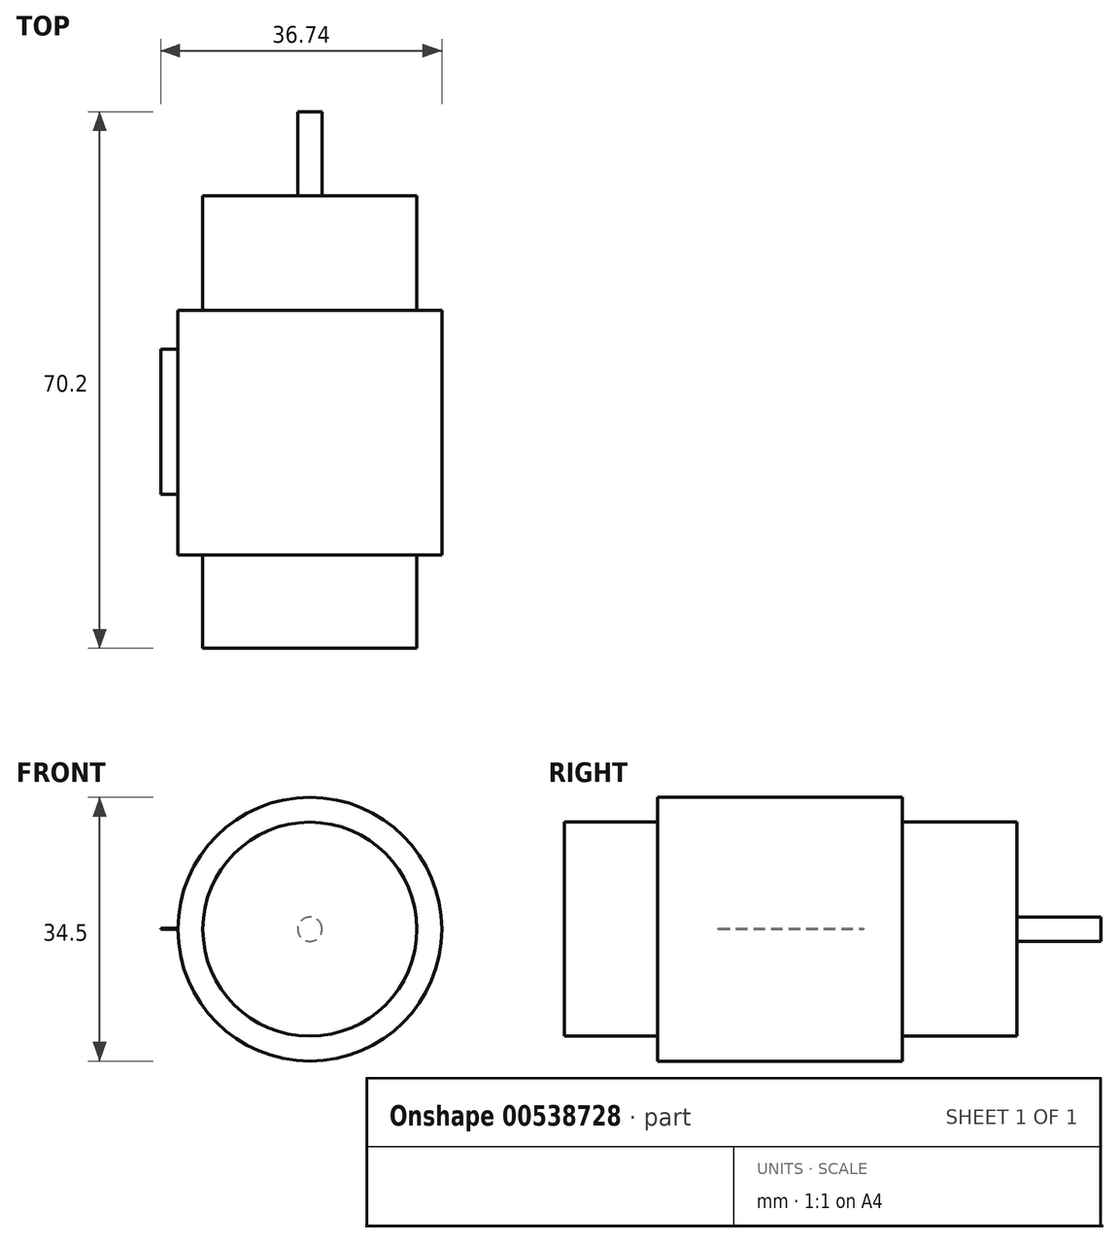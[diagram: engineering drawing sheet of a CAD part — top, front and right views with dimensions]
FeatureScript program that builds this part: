
annotation { "Feature Type Name" : "Feature", "Feature Type Description" : "" }
export const myFeature = defineFeature(function(context is Context, id is Id, definition is map)
    precondition{}
    {
        {
            var Q0;
            Q0=qCreatedBy(makeId("Front.planeOp"),FACE);
            var sketch = newSketch(context, id + "F0", { "sketchPlane" : qUnion([Q0])});
            skCircle(sketch, "E0", {"center": v(0, 0) * mm, "radius": 14 * mm});
            skSolve(sketch);
        }
        {
            var Q0;
            Q0=makeQuery(id+"F0.imprint","IMPRINT",FACE,{"disambiguationData":[TD([[makeQuery(id+"F0.imprint","IMPRINT",EDGE,{"derivedFrom":sQuery(id+"F0.wireOp",EDGE,"E0")}),1.0]])]});
            extrude(context, id + "F1", {"entities" : qUnion([Q0]), "depth" : 59.2 * mm, "offsetDistance" : 25 * mm});
        }
        {
            var Q0;
            Q0=qCreatedBy(makeId("Front.planeOp"),FACE);
            var sketch = newSketch(context, id + "F2", { "sketchPlane" : qUnion([Q0])});
            skCircle(sketch, "E1", {"center": v(0, 0) * mm, "radius": 17.25 * mm});
            skSolve(sketch);
        }
        {
            var Q0;
            Q0=makeQuery(id+"F2.imprint","IMPRINT",FACE,{"disambiguationData":[TD([[makeQuery(id+"F2.imprint","IMPRINT",EDGE,{"derivedFrom":sQuery(id+"F2.wireOp",EDGE,"E1")}),1.0]])]});
            extrude(context, id + "F3", {"entities" : qUnion([Q0]), "operationType" : NewBodyOperationType.ADD, "depth" : (15 + 32) * mm, "offsetDistance" : 25 * mm, "hasSecondDirection" : true, "secondDirectionOppositeDirection" : false, "secondDirectionDepth" : 15 * mm});
        }
        {
            var Q0;
            Q0=qCreatedBy(makeId("Front.planeOp"),FACE);
            var sketch = newSketch(context, id + "F4", { "sketchPlane" : qUnion([Q0])});
            skCircle(sketch, "E2", {"center": v(0, 0) * mm, "radius": 1.58 * mm});
            skSolve(sketch);
        }
        {
            var Q0;
            Q0=makeQuery(id+"F4.imprint","IMPRINT",FACE,{"disambiguationData":[TD([[makeQuery(id+"F4.imprint","IMPRINT",EDGE,{"derivedFrom":sQuery(id+"F4.wireOp",EDGE,"E2")}),1.0]])]});
            extrude(context, id + "F5", {"entities" : qUnion([Q0]), "operationType" : NewBodyOperationType.ADD, "oppositeDirection" : true, "depth" : 11 * mm, "offsetDistance" : 25 * mm});
        }
        {
            var Q0;
            Q0=qCreatedBy(makeId("Top.planeOp"),FACE);
            var sketch = newSketch(context, id + "F6", { "sketchPlane" : qUnion([Q0])});
            skLineSegment(sketch, "E3.bottom", {"start": v(-19.49, -39.03) * mm, "end": v(-15.1, -39.03) * mm});
            skLineSegment(sketch, "E3.top", {"start": v(-19.49, -20.07) * mm, "end": v(-15.1, -20.07) * mm});
            skLineSegment(sketch, "E3.left", {"start": v(-19.49, -39.03) * mm, "end": v(-19.49, -20.07) * mm});
            skLineSegment(sketch, "E3.right", {"start": v(-15.1, -39.03) * mm, "end": v(-15.1, -20.07) * mm});
            skSolve(sketch);
        }
        {
            var Q0;
            Q0=makeQuery(id+"F6.imprint","IMPRINT",FACE,{"disambiguationData":[TD([[makeQuery(id+"F6.imprint","IMPRINT",EDGE,{"derivedFrom":sQuery(id+"F6.wireOp",EDGE,"E3.bottom")}),1.0]])]});
            extrude(context, id + "F7", {"entities" : qUnion([Q0]), "operationType" : NewBodyOperationType.ADD, "depth" : .1 * mm, "offsetDistance" : 25 * mm});
        }
    });
